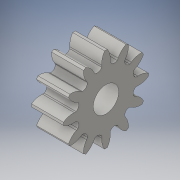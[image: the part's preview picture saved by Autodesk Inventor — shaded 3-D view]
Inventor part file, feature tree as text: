
AUTODESK INVENTOR PART (.ipt)
format: ipt  version: 2016 (Build 200138000, 138)  size: 275,968 bytes
history: native  units: in
note: dims shown in document units (in); Inventor stores cm internally (conversion verified against a paired STEP export)
features: extrude x3, sketch x3, plane x1
ambient origin geometry x8: Origin, YZ Plane, XZ Plane, XY Plane, X Axis, Y Axis, Z Axis, Center Point
bodies: Solid1 (feature_tree)
feature tree (7):
  plane  "Work Plane2"
  extrude  "Extrusion19"  Depth=0.2255in TaperAngle=0.0deg
  extrude  "Extrusion20"  Depth=100.0in TaperAngle=0.0deg
  extrude  "Extrusion21"  Depth=4.7244in TaperAngle=360.0deg
  sketch  "Sketch6"  dims[d92=4.7244in d94=360.0deg d102=0.2255in d103=0.0in]
  sketch  "Sketch7"  dims[d104=0.18in d105=100.0in d106=0.0in]
  sketch  "Sketch8"  dims[d107=0.4in d108=4.7244in d110=360.0deg d112=100.0in d113=0.0in]
